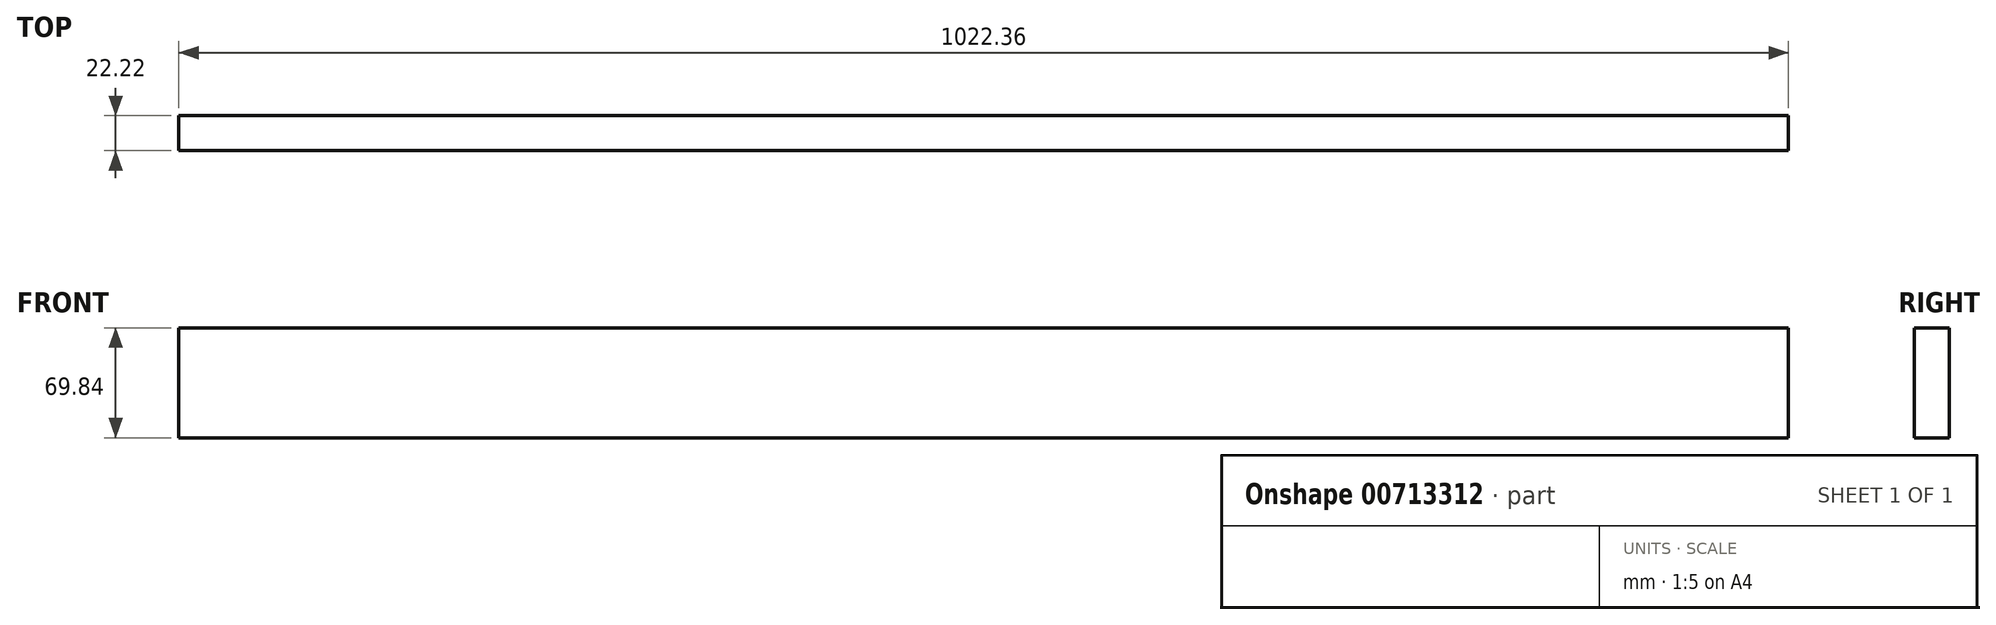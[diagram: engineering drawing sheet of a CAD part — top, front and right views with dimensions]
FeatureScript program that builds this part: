
annotation { "Feature Type Name" : "Feature", "Feature Type Description" : "" }
export const myFeature = defineFeature(function(context is Context, id is Id, definition is map)
    precondition{}
    {
        {
            var Q0;
            Q0=qCreatedBy(makeId("Top.planeOp"),FACE);
            var sketch = newSketch(context, id + "F0", { "sketchPlane" : qUnion([Q0])});
            skLineSegment(sketch, "E0.bottom", {"start": v(511.18, -11.11) * mm, "end": v(-511.18, -11.11) * mm});
            skLineSegment(sketch, "E0.top", {"start": v(511.18, 11.11) * mm, "end": v(-511.18, 11.11) * mm});
            skLineSegment(sketch, "E0.left", {"start": v(511.18, -11.11) * mm, "end": v(511.18, 11.11) * mm});
            skLineSegment(sketch, "E0.right", {"start": v(-511.18, -11.11) * mm, "end": v(-511.18, 11.11) * mm});
            skPoint(sketch, "E0.middle", {"position": v(0, 0) * mm});
            skSolve(sketch);
        }
        {
            var Q0;
            Q0 = qSketchRegion(id + "F0", true);
            extrude(context, id + "F1", {"entities" : qUnion([Q0]), "endBound" : BoundingType.SYMMETRIC, "depth" : 69.85 * mm, "offsetDistance" : 25.4 * mm});
        }
    });
